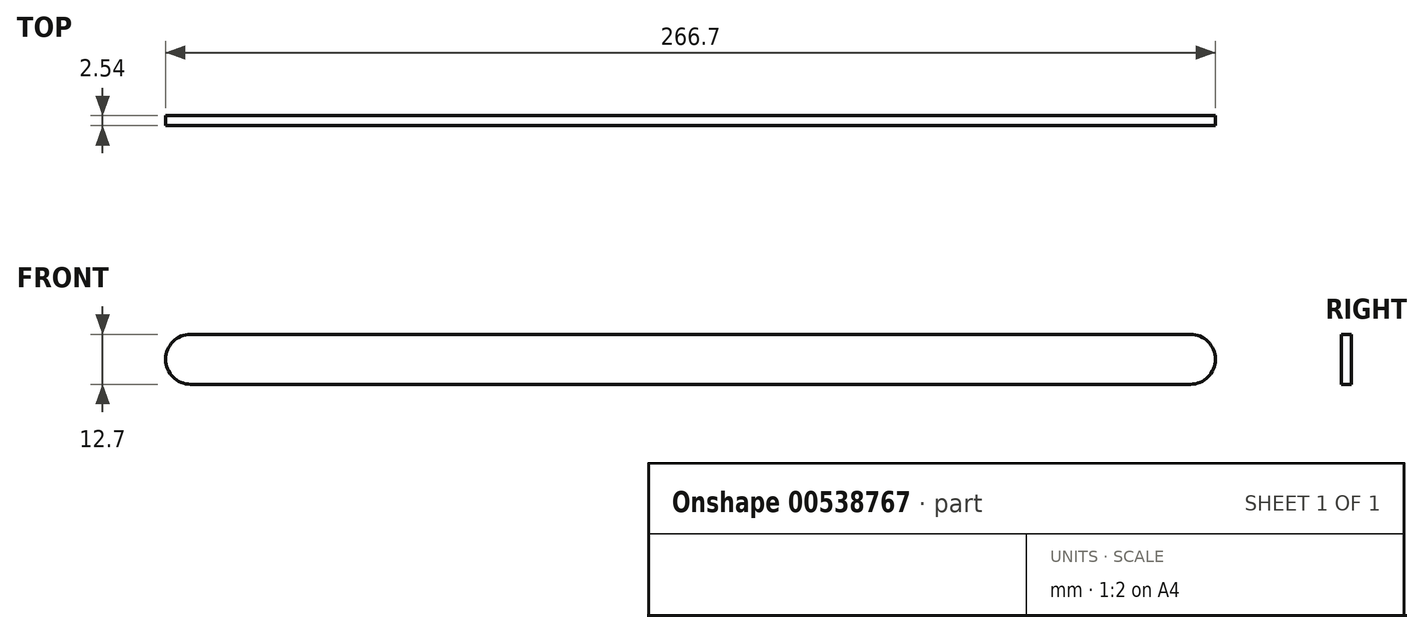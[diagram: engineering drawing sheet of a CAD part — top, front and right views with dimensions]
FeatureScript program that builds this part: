
annotation { "Feature Type Name" : "Feature", "Feature Type Description" : "" }
export const myFeature = defineFeature(function(context is Context, id is Id, definition is map)
    precondition{}
    {
        {
            var Q0;
            Q0=qCreatedBy(makeId("Front.planeOp"),FACE);
            var sketch = newSketch(context, id + "F0", { "sketchPlane" : qUnion([Q0])});
            skLineSegment(sketch, "E0", {"start": v(-127, 0) * mm, "end": v(127, 0) * mm});
            skLineSegment(sketch, "E1", {"start": v(-127, 6.35) * mm, "end": v(127, 6.35) * mm});
            skLineSegment(sketch, "E2", {"start": v(-127, -6.35) * mm, "end": v(127, -6.35) * mm});
            skArc(sketch, "E3", {"start": v(-127, 6.35) * mm, "mid": v(-133.35, 0) * mm, "end": v(-127, -6.35) * mm});
            skArc(sketch, "E4", {"start": v(127, 6.35) * mm, "mid": v(133.35, 0) * mm, "end": v(127, -6.35) * mm});
            skSolve(sketch);
        }
        {
            var Q0;
            Q0 = qSketchRegion(id + "F0", true);
            extrude(context, id + "F1", {"entities" : qUnion([Q0]), "endBound" : BoundingType.SYMMETRIC, "depth" : 2.54 * mm, "offsetDistance" : 25.4 * mm});
        }
    });
